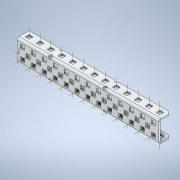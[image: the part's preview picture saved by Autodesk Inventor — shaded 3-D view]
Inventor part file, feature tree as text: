
AUTODESK INVENTOR PART (.ipt)
format: ipt  version: 2020 (Build 240168000, 168)  size: 1,273,856 bytes
history: native  units: in
note: dims shown in document units (in); Inventor stores cm internally (conversion verified against a paired STEP export)
features: other x68, plane x8, pattern_linear x4, split x2, sheet_metal_op x1
ambient origin geometry x8: Origin, YZ Plane, XZ Plane, XY Plane, X Axis, Y Axis, Z Axis, Center Point
bodies: Solid1 (feature_tree)
feature tree (83):
  other  "Work Axis1"
  pattern_linear  "Rectangular Pattern1"  Count1=13 Spacing1=0.5in
  other  "Work Axis72"
  pattern_linear  "Rectangular Pattern2"  Count1=13 Spacing1=0.5in
  pattern_linear  "Rectangular Pattern3"  Count1=13 Spacing1=0.5in
  other  "Work Axis141"
  pattern_linear  "Rectangular Pattern4"  Count1=12 Spacing1=0.5in
  plane  "Work Plane7"
  split  "Split1"
  plane  "Work Plane8"
  split  "Split2"
  plane  "Work Plane1"
  plane  "Work Plane2"
  other  "Work Point1"
  other  "Work Axis2"
  other  "Work Axis3"
  other  "Work Axis36"
  other  "Work Axis37"
  other  "Work Axis38"
  plane  "Work Plane3"
  plane  "Work Plane4"
  other  "Work Point2"
  other  "Work Axis71"
  other  "Work Point3"
  other  "Work Axis73"
  other  "Work Axis74"
  other  "Work Axis75"
  other  "Work Axis76"
  other  "Work Axis77"
  other  "Work Axis78"
  other  "Work Axis79"
  other  "Work Axis80"
  other  "Work Axis81"
  other  "Work Axis82"
  other  "Work Axis83"
  other  "Work Axis84"
  other  "Work Axis107"
  other  "Work Axis108"
  other  "Work Axis109"
  other  "Work Axis110"
  plane  "Work Plane5"
  plane  "Work Plane6"
  other  "Work Point4"
  other  "Work Axis142"
  other  "Work Axis143"
  other  "Work Axis144"
  other  "Work Axis145"
  other  "Work Axis146"
  other  "Work Axis147"
  other  "Work Axis148"
  other  "Work Axis149"
  other  "Work Axis150"
  other  "Work Axis151"
  other  "Work Axis152"
  other  "Work Axis175"
  other  "Work Axis176"
  other  "Work Axis177"
  other  "Work Axis178"
  other  "Work Axis179"
  other  "Work Axis180"
  other  "Work Axis181"
  other  "Work Axis182"
  other  "Work Axis185"
  other  "Work Axis186"
  other  "Work Axis187"
  other  "Work Axis188"
  other  "Work Axis189"
  other  "Work Axis190"
  other  "Work Axis191"
  other  "Work Axis192"
  other  "Work Axis193"
  other  "Work Axis194"
  other  "Work Axis195"
  other  "Work Axis196"
  other  "Work Axis197"
  other  "Work Axis198"
  other  "Work Axis199"
  other  "Work Axis200"
  other  "Work Axis201"
  other  "Work Axis202"
  other  "Work Axis203"
  other  "Work Axis204"
  sheet_metal_op  "Fold1"
